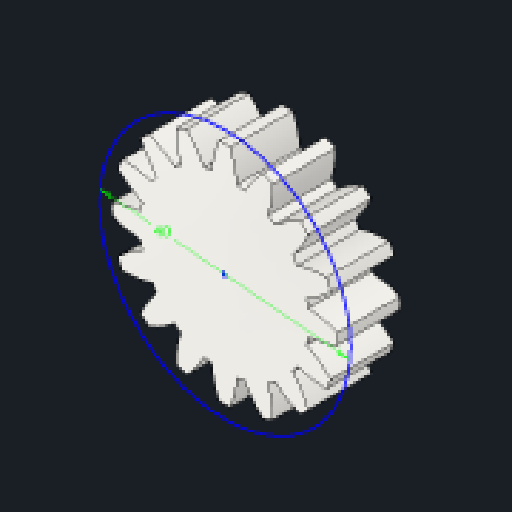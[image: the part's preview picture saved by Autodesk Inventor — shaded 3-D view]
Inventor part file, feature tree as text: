
AUTODESK INVENTOR PART (.ipt)
format: ipt  version: 2023.2 (Build 272271030, 271C)  size: 199,168 bytes
history: native  units: mm (DEFAULTED — no unit token found)
features: plane x3, other x3, sketch x3, extrude x1
ambient origin geometry x8: Origin, YZ Plane, XZ Plane, XY Plane, X Axis, Y Axis, Z Axis, Center Point
bodies: Solid1 (feature_tree)
feature tree (10):
  extrude  "Extrusion1"  Depth=10.0mm TaperAngle=0.0deg
  plane  "Work Plane2"
  plane  "Work Plane8"
  plane  "Work Plane9"
  other  "Spur Gear"
  sketch  "Sketch3"  dims[d4=10.0mm d5=0.0mm d16=51.0mm d17=0.0mm d34=1.963495mm d39=0.0mm d41=0.0mm d43=51.0mm d46=51.0mm d47=0.0mm d48=0.0mm d49=40.0mm]
  sketch  "Sketch1"  dims[d0=36.0mm d1=10.0mm d2=0.0mm]
  sketch  "Sketch2"  dims[d3=32.0mm]
  other  "Srf1"
  other  "Pitch Diameter"
